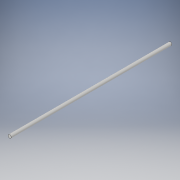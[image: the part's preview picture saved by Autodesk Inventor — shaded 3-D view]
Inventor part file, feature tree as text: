
AUTODESK INVENTOR PART (.ipt)
format: ipt  version: 2018 (Build 220112000, 112)  size: 93,184 bytes
history: native  units: in
note: dims shown in document units (in); Inventor stores cm internally (conversion verified against a paired STEP export)
features: revolve x1, sketch x1
ambient origin geometry x8: Origin, YZ Plane, XZ Plane, XY Plane, X Axis, Y Axis, Z Axis, Center Point
bodies: Solid1 (feature_tree)
feature tree (2):
  revolve  "Revolution1"  [1 undecoded]
  sketch  "Sketch1"  dims[d0=0.1575in d1=15.748in d2=90.0deg]
note: 1 required parameter value undecoded (feature->parameter linkage not recoverable at this tier; creation-order binding heuristic only, values carry confidence <= 0.55)
